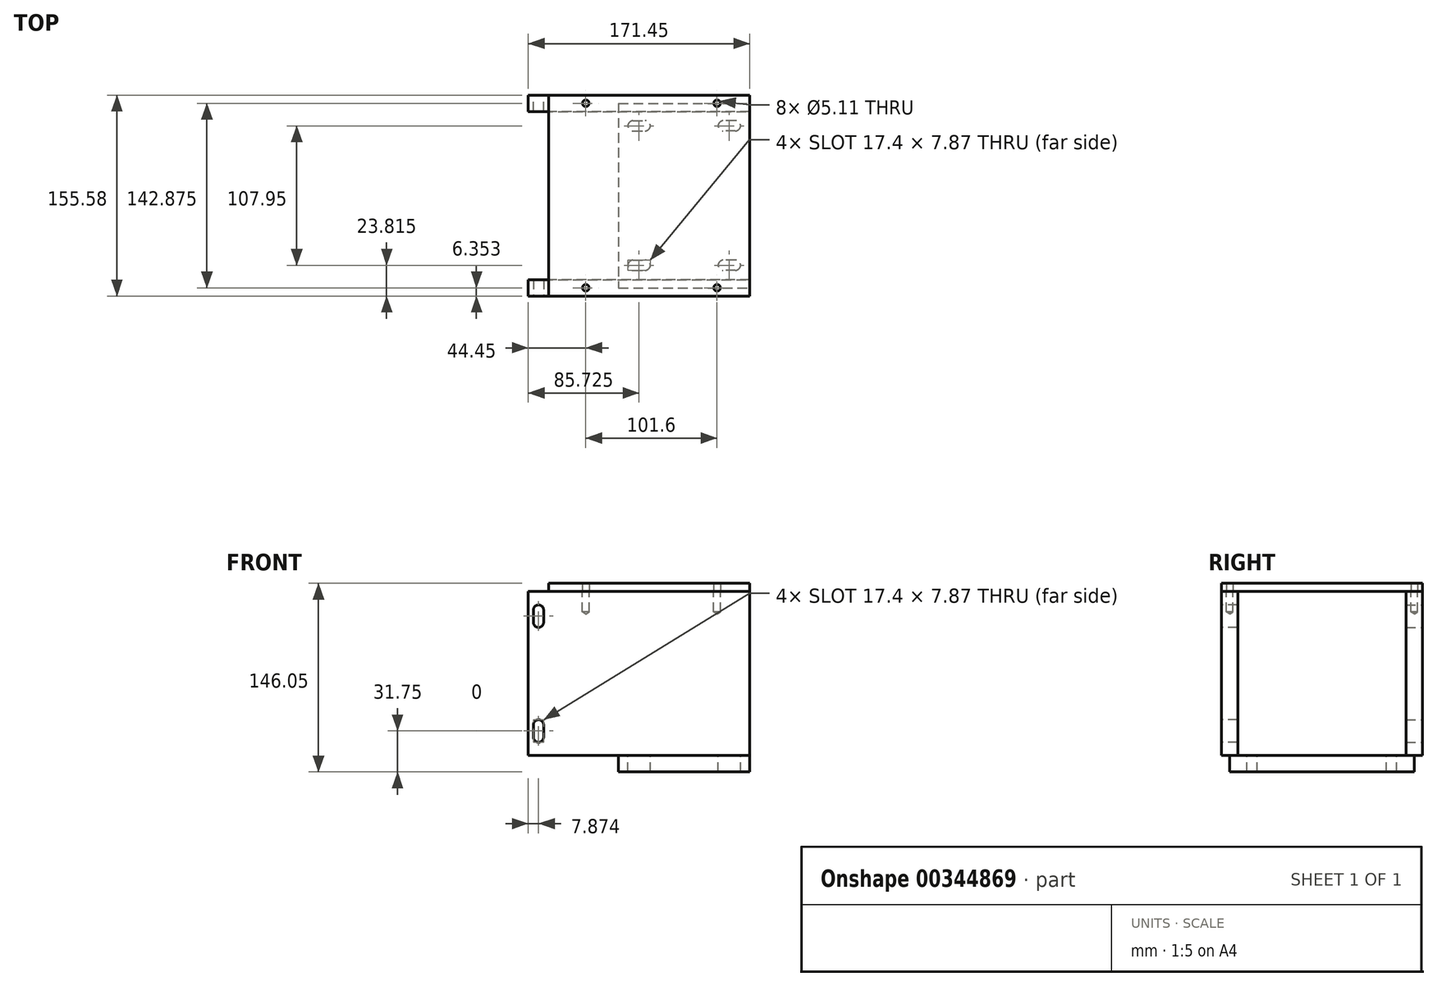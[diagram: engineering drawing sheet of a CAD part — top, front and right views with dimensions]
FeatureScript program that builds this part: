
annotation { "Feature Type Name" : "Feature", "Feature Type Description" : "" }
export const myFeature = defineFeature(function(context is Context, id is Id, definition is map)
    precondition{}
    {
        {
            var Q0;
            Q0=qCreatedBy(makeId("Top.planeOp"),FACE);
            var sketch = newSketch(context, id + "F0", { "sketchPlane" : qUnion([Q0])});
            skLineSegment(sketch, "E0.bottom", {"start": v(-50.8, 71.44) * mm, "end": v(50.8, 71.44) * mm});
            skLineSegment(sketch, "E0.top", {"start": v(-50.8, -71.44) * mm, "end": v(50.8, -71.44) * mm});
            skLineSegment(sketch, "E0.left", {"start": v(-50.8, 71.44) * mm, "end": v(-50.8, -71.44) * mm});
            skLineSegment(sketch, "E0.right", {"start": v(50.8, 71.44) * mm, "end": v(50.8, -71.44) * mm});
            skPoint(sketch, "E0.middle", {"position": v(0, 0) * mm});
            skSolve(sketch);
        }
        {
            var Q0;
            Q0 = qSketchRegion(id + "F0", true);
            extrude(context, id + "F1", {"entities" : qUnion([Q0]), "oppositeDirection" : true, "depth" : 12.7 * mm});
        }
        {
            var Q0;
            Q0=makeQuery(id+"F1.opExtrude","CAP_FACE",FACE,{"disambiguationData":[OSD([sQuery(id+"F0.wireOp",EDGE,"E0.bottom"),sQuery(id+"F0.wireOp",EDGE,"E0.top"),sQuery(id+"F0.wireOp",EDGE,"E0.left"),sQuery(id+"F0.wireOp",EDGE,"E0.right")])],"isStart":true});
            var sketch = newSketch(context, id + "F2", { "sketchPlane" : qUnion([Q0])});
            skLineSegment(sketch, "E1", {"start": v(-110.76, 0) * mm, "end": v(98.43, 0) * mm, "construction": true});
            skLineSegment(sketch, "E2", {"start": v(0, 111.96) * mm, "end": v(0, -90.73) * mm, "construction": true});
            skPoint(sketch, "E2.endSnap0", {"position": v(0, 71.44) * mm});
            skLineSegment(sketch, "E3.0", {"start": v(-34.93, 111.96) * mm, "end": v(-34.92, -90.73) * mm, "construction": true});
            skLineSegment(sketch, "E4", {"start": v(-39.69, -53.98) * mm, "end": v(-30.16, -53.98) * mm});
            skArc(sketch, "E5.0.startCap", {"start": v(-39.69, -57.91) * mm, "mid": v(-43.62, -53.98) * mm, "end": v(-39.69, -50.04) * mm});
            skArc(sketch, "E5.0.endCap", {"start": v(-30.16, -50.04) * mm, "mid": v(-26.23, -53.98) * mm, "end": v(-30.16, -57.91) * mm});
            skLineSegment(sketch, "E5.0.left", {"start": v(-39.69, -50.04) * mm, "end": v(-30.16, -50.04) * mm});
            skLineSegment(sketch, "E5.0.right", {"start": v(-39.69, -57.91) * mm, "end": v(-30.16, -57.91) * mm});
            skLineSegment(sketch, "E6.MirrorCS", {"start": v(39.69, -57.91) * mm, "end": v(30.16, -57.91) * mm});
            skLineSegment(sketch, "E7.MirrorCS", {"start": v(39.69, -53.97) * mm, "end": v(30.16, -53.97) * mm});
            skArc(sketch, "E8.MirrorCS", {"start": v(39.69, -57.91) * mm, "mid": v(43.62, -53.97) * mm, "end": v(39.69, -50.04) * mm});
            skArc(sketch, "E9.MirrorCS", {"start": v(30.16, -50.04) * mm, "mid": v(26.23, -53.97) * mm, "end": v(30.16, -57.91) * mm});
            skLineSegment(sketch, "E10.MirrorCS", {"start": v(39.69, -50.04) * mm, "end": v(30.16, -50.04) * mm});
            skLineSegment(sketch, "E11.MirrorCS", {"start": v(-39.69, 50.04) * mm, "end": v(-30.16, 50.04) * mm});
            skArc(sketch, "E12.MirrorCS", {"start": v(-30.16, 50.04) * mm, "mid": v(-26.23, 53.98) * mm, "end": v(-30.16, 57.91) * mm});
            skArc(sketch, "E13.MirrorCS", {"start": v(-39.69, 57.91) * mm, "mid": v(-43.62, 53.98) * mm, "end": v(-39.69, 50.04) * mm});
            skLineSegment(sketch, "E14.MirrorCS", {"start": v(-39.69, 53.98) * mm, "end": v(-30.16, 53.98) * mm});
            skArc(sketch, "E15.MirrorCS", {"start": v(39.69, 57.91) * mm, "mid": v(43.62, 53.97) * mm, "end": v(39.69, 50.04) * mm});
            skLineSegment(sketch, "E16.MirrorCS", {"start": v(39.69, 53.97) * mm, "end": v(30.16, 53.97) * mm});
            skLineSegment(sketch, "E17.MirrorCS", {"start": v(39.69, 57.91) * mm, "end": v(30.16, 57.91) * mm});
            skLineSegment(sketch, "E18.MirrorCS", {"start": v(39.69, 50.04) * mm, "end": v(30.16, 50.04) * mm});
            skLineSegment(sketch, "E19.MirrorCS", {"start": v(-39.69, 57.91) * mm, "end": v(-30.16, 57.91) * mm});
            skArc(sketch, "E20.MirrorCS", {"start": v(30.16, 50.04) * mm, "mid": v(26.23, 53.97) * mm, "end": v(30.16, 57.91) * mm});
            skSolve(sketch);
        }
        {
            var Q0;
            Q0 = qSketchRegion(id + "F2", true);
            extrude(context, id + "F3", {"entities" : qUnion([Q0]), "operationType" : NewBodyOperationType.REMOVE, "endBound" : BoundingType.THROUGH_ALL, "oppositeDirection" : true, "depth" : 25.4 * mm});
        }
        {
            var Q0;
            Q0=makeQuery(id+"F1.opExtrude","SWEPT_FACE",FACE,{"disambiguationData":[OSD([sQuery(id+"F0.wireOp",EDGE,"E0.top")])]});
            var sketch = newSketch(context, id + "F4", { "sketchPlane" : qUnion([Q0])});
            skLineSegment(sketch, "E21.0", {"start": v(50.8, -12.7) * mm, "end": v(50.8, 0) * mm, "construction": true});
            skLineSegment(sketch, "E22.bottom", {"start": v(50.8, 0) * mm, "end": v(-120.65, 0) * mm});
            skLineSegment(sketch, "E22.top", {"start": v(50.8, 127) * mm, "end": v(-120.65, 127) * mm});
            skLineSegment(sketch, "E22.left", {"start": v(50.8, 0) * mm, "end": v(50.8, 127) * mm});
            skLineSegment(sketch, "E22.right", {"start": v(-120.65, 0) * mm, "end": v(-120.65, 127) * mm});
            skSolve(sketch);
        }
        {
            var Q0;
            Q0 = qSketchRegion(id + "F4", true);
            extrude(context, id + "F5", {"entities" : qUnion([Q0]), "endBound" : BoundingType.SYMMETRIC, "depth" : 12.7 * mm});
        }
        {
            var Q0;
            Q0=makeQuery(id+"F5.opExtrude","CAP_FACE",FACE,{"disambiguationData":[OSD([sQuery(id+"F4.wireOp",EDGE,"E22.bottom"),sQuery(id+"F4.wireOp",EDGE,"E22.top"),sQuery(id+"F4.wireOp",EDGE,"E22.left"),sQuery(id+"F4.wireOp",EDGE,"E22.right")])],"isStart":false});
            var sketch = newSketch(context, id + "F6", { "sketchPlane" : qUnion([Q0])});
            skLineSegment(sketch, "E23.0", {"start": v(-112.78, 0) * mm, "end": v(-112.78, 127) * mm, "construction": true});
            skLineSegment(sketch, "E24.0", {"start": v(50.8, 107.95) * mm, "end": v(-120.65, 107.95) * mm, "construction": true});
            skLineSegment(sketch, "E25.0", {"start": v(50.8, 19.05) * mm, "end": v(-120.65, 19.05) * mm, "construction": true});
            skLineSegment(sketch, "E26", {"start": v(-112.78, 63.5) * mm, "end": v(-152.81, 63.5) * mm, "construction": true});
            skLineSegment(sketch, "E27", {"start": v(-112.78, 112.71) * mm, "end": v(-112.78, 103.19) * mm});
            skArc(sketch, "E28.0.endCap", {"start": v(-108.84, 103.19) * mm, "mid": v(-112.78, 99.25) * mm, "end": v(-116.71, 103.19) * mm});
            skLineSegment(sketch, "E28.0.left", {"start": v(-108.84, 112.71) * mm, "end": v(-108.84, 103.19) * mm});
            skLineSegment(sketch, "E28.0.right", {"start": v(-116.71, 112.71) * mm, "end": v(-116.71, 103.19) * mm});
            skArc(sketch, "E29.MirrorCS", {"start": v(-108.84, 112.71) * mm, "mid": v(-112.78, 116.65) * mm, "end": v(-116.71, 112.71) * mm});
            skLineSegment(sketch, "E30.MirrorCS", {"start": v(-112.78, 14.29) * mm, "end": v(-112.78, 23.81) * mm});
            skLineSegment(sketch, "E31.MirrorCS", {"start": v(-108.84, 14.29) * mm, "end": v(-108.84, 23.81) * mm});
            skArc(sketch, "E32.MirrorCS", {"start": v(-108.84, 23.81) * mm, "mid": v(-112.78, 27.75) * mm, "end": v(-116.71, 23.81) * mm});
            skLineSegment(sketch, "E33.MirrorCS", {"start": v(-116.71, 14.29) * mm, "end": v(-116.71, 23.81) * mm});
            skArc(sketch, "E34.MirrorCS", {"start": v(-108.84, 14.29) * mm, "mid": v(-112.78, 10.35) * mm, "end": v(-116.71, 14.29) * mm});
            skSolve(sketch);
        }
        {
            var Q0;
            Q0 = qSketchRegion(id + "F6", true);
            extrude(context, id + "F7", {"entities" : qUnion([Q0]), "operationType" : NewBodyOperationType.REMOVE, "endBound" : BoundingType.THROUGH_ALL, "oppositeDirection" : true, "depth" : 25.4 * mm});
        }
        {
            var Q0;
            Q0=makeQuery(id+"F5.opExtrude","SWEPT_FACE",FACE,{"disambiguationData":[OSD([sQuery(id+"F4.wireOp",EDGE,"E22.top")])]});
            var sketch = newSketch(context, id + "F8", { "sketchPlane" : qUnion([Q0])});
            skLineSegment(sketch, "E35.0", {"start": v(25.4, -77.79) * mm, "end": v(25.4, -65.09) * mm, "construction": true});
            skLineSegment(sketch, "E36.0", {"start": v(-76.2, -77.79) * mm, "end": v(-76.2, -65.09) * mm, "construction": true});
            skLineSegment(sketch, "E37", {"start": v(50.8, -71.44) * mm, "end": v(-82.63, -71.44) * mm, "construction": true});
            skPoint(sketch, "E38", {"position": v(-76.2, -71.44) * mm});
            skPoint(sketch, "E39", {"position": v(25.4, -71.44) * mm});
            skSolve(sketch);
        }
        {
            var Q0;
            Q0=sQuery(id+"F8.wireOp",VERTEX,"E38");
            var Q1;
            Q1=sQuery(id+"F8.wireOp",VERTEX,"E39");
            var Q2;
            Q2=makeQuery(id+"F5.opExtrude","SWEPT_BODY",BODY,{"disambiguationData":[OSD([sQuery(id+"F4.wireOp",EDGE,"E22.bottom"),sQuery(id+"F4.wireOp",EDGE,"E22.top"),sQuery(id+"F4.wireOp",EDGE,"E22.left"),sQuery(id+"F4.wireOp",EDGE,"E22.right")])]});
            hole(context, id + "F9", {"style" : HoleStyle.SIMPLE, "endStyle" : HoleEndStyle.BLIND, "standardTappedOrClearance" : lookupTablePath({ "standard" : "ANSI", "engagement" : "75%", "pitch" : "20 tpi", "size" : "1/4", "type" : "Tapped" }), "standardBlindInLast" : lookupTablePath({ "standard" : "ANSI", "engagement" : "75%", "pitch" : "20 tpi", "size" : "1/4", "type" : "Tapped" }), "holeDiameter" : 5.1 * mm, "showTappedDepth" : true, "holeDepth" : 15.88 * mm, "isTappedThrough" : true, "tappedDepth" : 12.06 * mm, "tapClearance" : 3, "locations" : qUnion([Q0, Q1]), "scope" : qUnion([Q2]), "majorDiameter" : 6.35 * mm});
        }
        {
            var Q0;
            Q0=makeQuery(id+"F5.opExtrude","SWEPT_BODY",BODY,{"disambiguationData":[OSD([sQuery(id+"F4.wireOp",EDGE,"E22.bottom"),sQuery(id+"F4.wireOp",EDGE,"E22.top"),sQuery(id+"F4.wireOp",EDGE,"E22.left"),sQuery(id+"F4.wireOp",EDGE,"E22.right")])]});
            var Q1;
            Q1=qCreatedBy(makeId("Front.planeOp"),FACE);
            mirror(context, id + "F10", {"entities" : qUnion([Q0]), "mirrorPlane" : qUnion([Q1])});
        }
        {
            var Q0;
            Q0=makeQuery(id+"F5.opExtrude","SWEPT_FACE",FACE,{"disambiguationData":[OSD([sQuery(id+"F4.wireOp",EDGE,"E22.top")])]});
            var sketch = newSketch(context, id + "F11", { "sketchPlane" : qUnion([Q0])});
            skLineSegment(sketch, "E40.0", {"start": v(-104.78, -77.79) * mm, "end": v(-104.78, -65.09) * mm, "construction": true});
            skLineSegment(sketch, "E41.0", {"start": v(50.8, 77.79) * mm, "end": v(-120.65, 77.79) * mm, "construction": true});
            skLineSegment(sketch, "E42.bottom", {"start": v(-104.78, -77.79) * mm, "end": v(50.8, -77.79) * mm});
            skLineSegment(sketch, "E42.top", {"start": v(-104.78, 77.79) * mm, "end": v(50.8, 77.79) * mm});
            skLineSegment(sketch, "E42.left", {"start": v(-104.78, -77.79) * mm, "end": v(-104.78, 77.79) * mm});
            skLineSegment(sketch, "E42.right", {"start": v(50.8, -77.79) * mm, "end": v(50.8, 77.79) * mm});
            skCircle(sketch, "E43.0", {"center": v(-76.2, 71.44) * mm, "radius": 2.55 * mm});
            skCircle(sketch, "E44.0", {"center": v(25.4, 71.44) * mm, "radius": 2.55 * mm});
            skCircle(sketch, "E45.0", {"center": v(25.4, -71.44) * mm, "radius": 2.55 * mm});
            skCircle(sketch, "E46.0", {"center": v(-76.2, -71.44) * mm, "radius": 2.55 * mm});
            skSolve(sketch);
        }
        {
            var Q0;
            Q0 = qSketchRegion(id + "F11", true);
            extrude(context, id + "F12", {"entities" : qUnion([Q0]), "depth" : 6.35 * mm});
        }
    });
